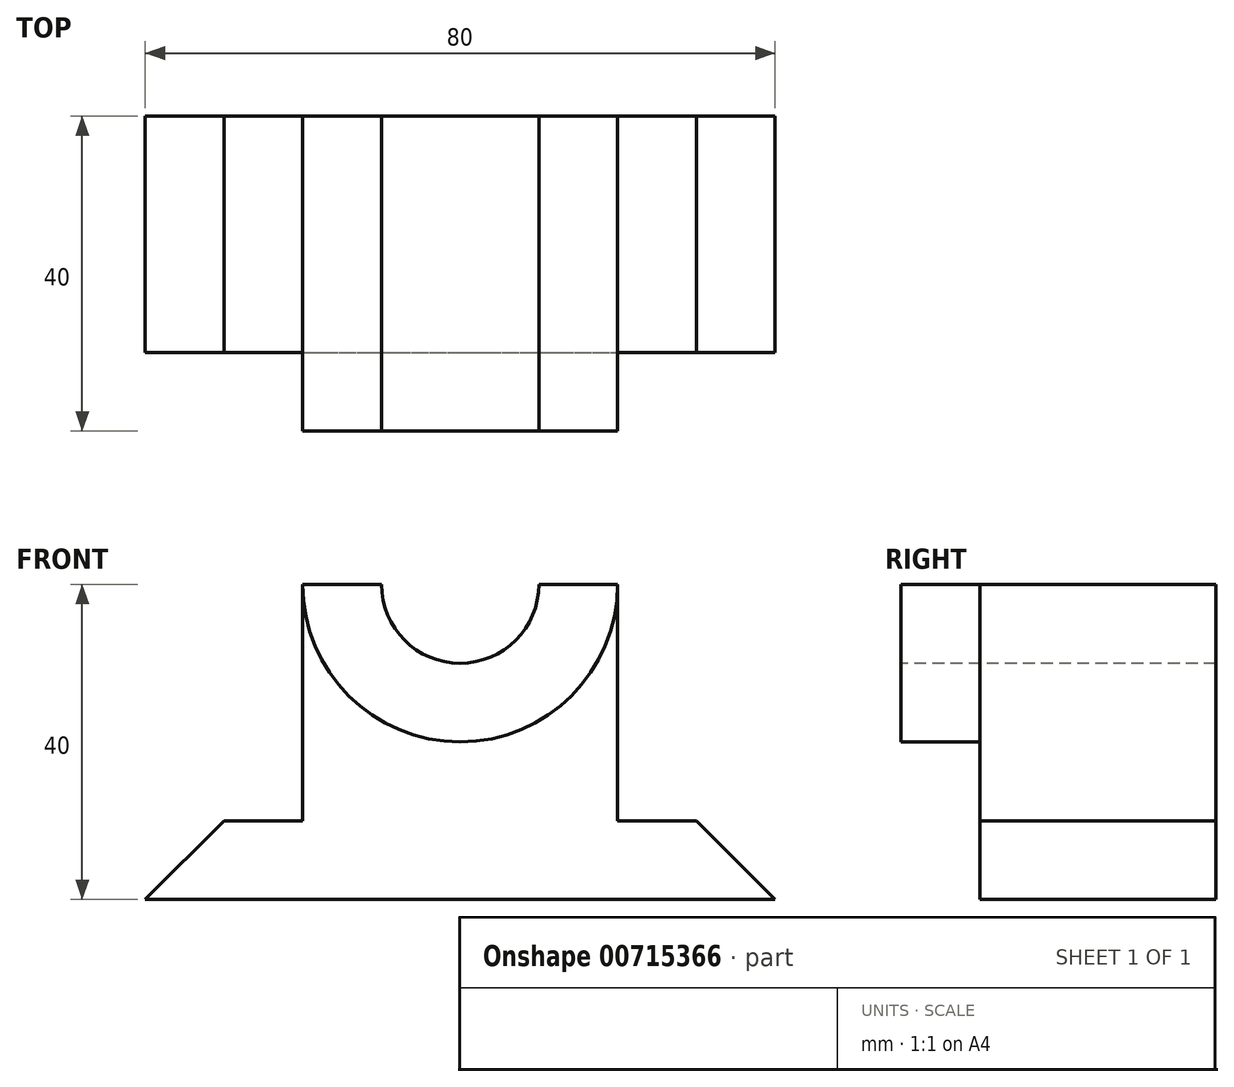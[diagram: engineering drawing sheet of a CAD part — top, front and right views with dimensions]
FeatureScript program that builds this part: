
annotation { "Feature Type Name" : "Feature", "Feature Type Description" : "" }
export const myFeature = defineFeature(function(context is Context, id is Id, definition is map)
    precondition{}
    {
        {
            var Q0;
            Q0=qCreatedBy(makeId("Front.planeOp"),FACE);
            var sketch = newSketch(context, id + "F0", { "sketchPlane" : qUnion([Q0])});
            skLineSegment(sketch, "E0", {"start": v(0, 0) * mm, "end": v(80, 0) * mm});
            skLineSegment(sketch, "E1", {"start": v(80, 0) * mm, "end": v(70, 10) * mm});
            skLineSegment(sketch, "E2", {"start": v(70, 10) * mm, "end": v(60, 10) * mm});
            skLineSegment(sketch, "E3", {"start": v(60, 10) * mm, "end": v(60, 40) * mm});
            skLineSegment(sketch, "E4", {"start": v(20, 10) * mm, "end": v(10, 10) * mm});
            skLineSegment(sketch, "E5", {"start": v(10, 10) * mm, "end": v(0, 0) * mm});
            skLineSegment(sketch, "E6", {"start": v(60, 40) * mm, "end": v(20, 40) * mm});
            skLineSegment(sketch, "E7", {"start": v(20, 40) * mm, "end": v(20, 10) * mm});
            skSolve(sketch);
        }
        {
            var Q0;
            Q0=makeQuery(id+"F0.imprint","IMPRINT",FACE,{"disambiguationData":[TD([[makeQuery(id+"F0.imprint","IMPRINT",EDGE,{"derivedFrom":sQuery(id+"F0.wireOp",EDGE,"E0")}),1.0]])]});
            extrude(context, id + "F1", {"entities" : qUnion([Q0]), "depth" : 30 * mm, "offsetDistance" : 25 * mm});
        }
        {
            var Q0;
            Q0=makeQuery(id+"F1.opExtrude","CAP_FACE",FACE,{"disambiguationData":[OSD([sQuery(id+"F0.wireOp",EDGE,"E0"),sQuery(id+"F0.wireOp",EDGE,"E1"),sQuery(id+"F0.wireOp",EDGE,"E2"),sQuery(id+"F0.wireOp",EDGE,"E3"),sQuery(id+"F0.wireOp",EDGE,"E4"),sQuery(id+"F0.wireOp",EDGE,"E5"),sQuery(id+"F0.wireOp",EDGE,"E6"),sQuery(id+"F0.wireOp",EDGE,"E7")])],"isStart":false});
            var sketch = newSketch(context, id + "F2", { "sketchPlane" : qUnion([Q0])});
            skArc(sketch, "E8", {"start": v(60, 40) * mm, "mid": v(40, 20) * mm, "end": v(20, 40) * mm});
            skLineSegment(sketch, "E9", {"start": v(20, 40) * mm, "end": v(60, 40) * mm});
            skSolve(sketch);
        }
        {
            var Q0;
            Q0=qSketchRegion(id+"F2",true);
            extrude(context, id + "F3", {"entities" : qUnion([Q0]), "operationType" : NewBodyOperationType.ADD, "depth" : 10 * mm, "offsetDistance" : 25 * mm});
        }
        {
            var Q0;
            Q0=makeQuery(id+"F3.opExtrude","CAP_FACE",FACE,{"disambiguationData":[OSD([sQuery(id+"F2.wireOp",EDGE,"E8"),sQuery(id+"F2.wireOp",EDGE,"E9")])],"isStart":false});
            var sketch = newSketch(context, id + "F4", { "sketchPlane" : qUnion([Q0])});
            skArc(sketch, "E10", {"start": v(50, 40) * mm, "mid": v(40, 30) * mm, "end": v(30, 40) * mm});
            skLineSegment(sketch, "E11", {"start": v(30, 40) * mm, "end": v(50, 40) * mm});
            skSolve(sketch);
        }
        {
            var Q0;
            Q0=qSketchRegion(id+"F4",true);
            extrude(context, id + "F5", {"entities" : qUnion([Q0]), "operationType" : NewBodyOperationType.REMOVE, "endBound" : BoundingType.THROUGH_ALL, "oppositeDirection" : true, "depth" : 25 * mm, "offsetDistance" : 25 * mm});
        }
    });
